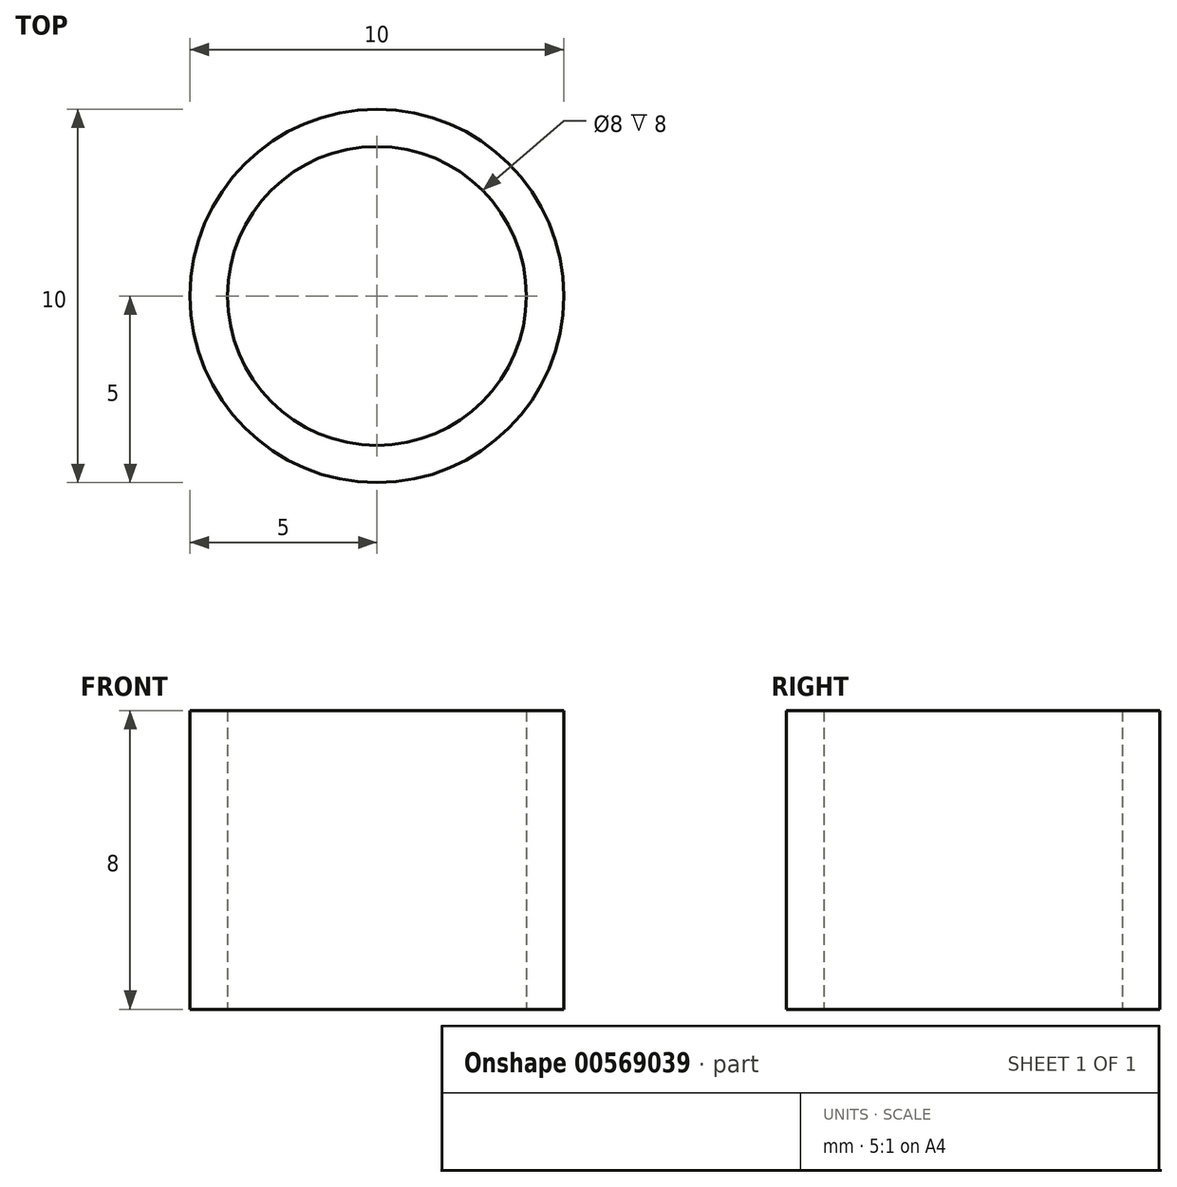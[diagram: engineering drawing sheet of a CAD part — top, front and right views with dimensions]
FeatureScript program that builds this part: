
annotation { "Feature Type Name" : "Feature", "Feature Type Description" : "" }
export const myFeature = defineFeature(function(context is Context, id is Id, definition is map)
    precondition{}
    {
        {
            var Q0;
            Q0=qCreatedBy(makeId("Top.planeOp"),FACE);
            var sketch = newSketch(context, id + "F0", { "sketchPlane" : qUnion([Q0])});
            skCircle(sketch, "E0", {"center": v(0, 0) * mm, "radius": 4 * mm});
            skCircle(sketch, "E1", {"center": v(0, 0) * mm, "radius": 5 * mm});
            skSolve(sketch);
        }
        {
            var Q0;
            Q0 = qSketchRegion(id + "F0", true);
            extrude(context, id + "F1", {"entities" : qUnion([Q0]), "depth" : 8 * mm, "offsetDistance" : 25 * mm});
        }
    });
